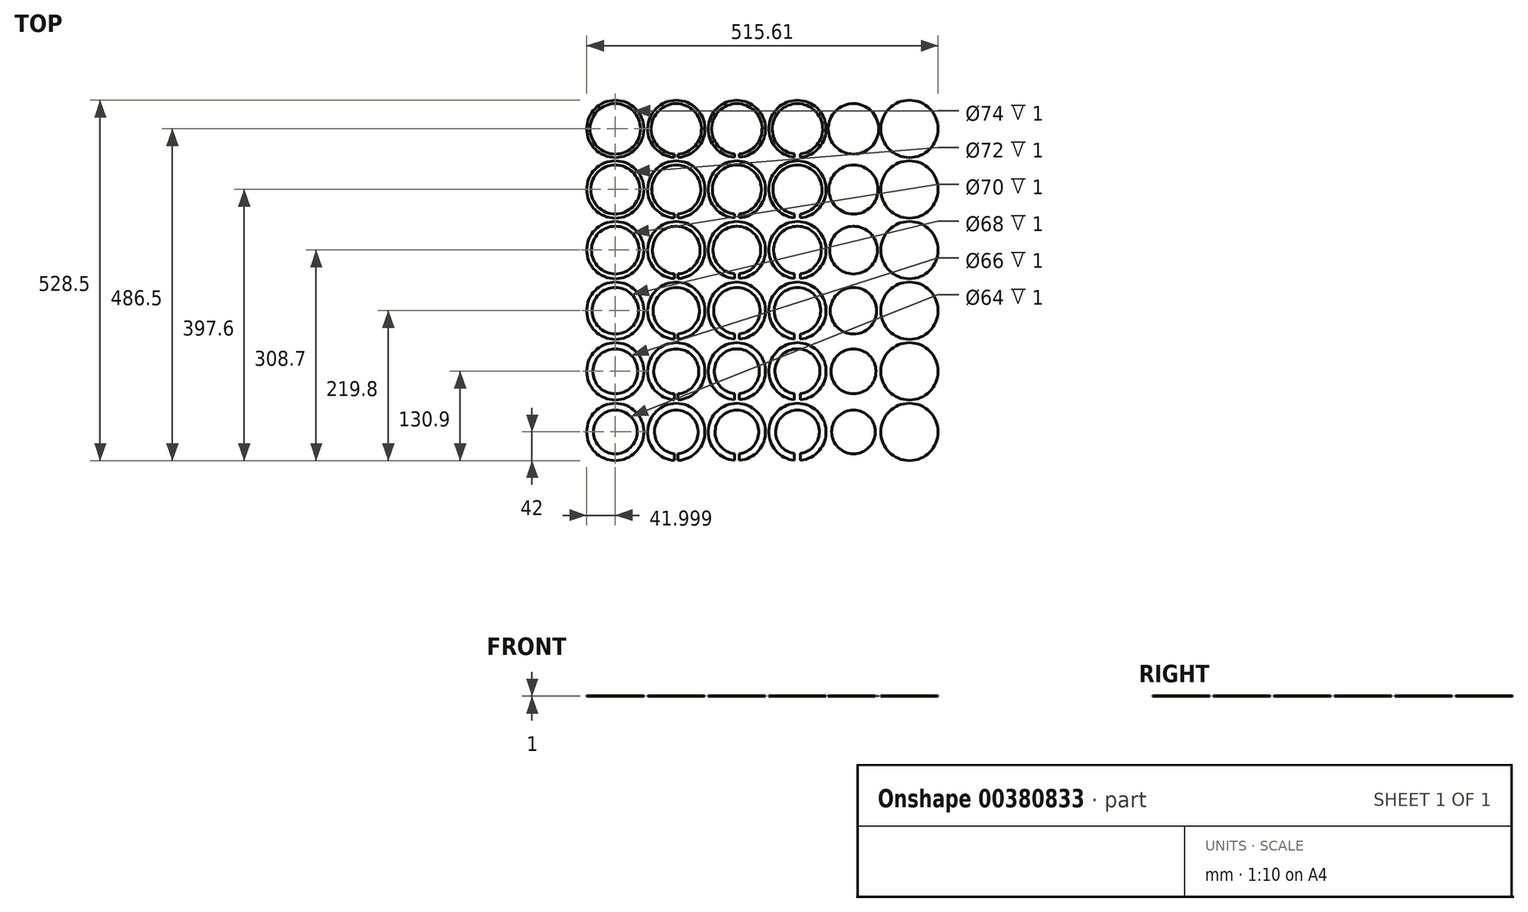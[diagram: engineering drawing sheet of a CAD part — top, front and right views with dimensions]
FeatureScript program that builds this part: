
annotation { "Feature Type Name" : "Feature", "Feature Type Description" : "" }
export const myFeature = defineFeature(function(context is Context, id is Id, definition is map)
    precondition{}
    {
        {
            var Q0;
            Q0=qCreatedBy(makeId("Top.planeOp"),FACE);
            var sketch = newSketch(context, id + "F0", { "sketchPlane" : qUnion([Q0])});
            skArc(sketch, "E0", {"start": v(2.5, -41.93) * mm, "mid": v(0, 42) * mm, "end": v(-2.5, -41.93) * mm});
            skArc(sketch, "E1", {"start": v(2.5, -36.92) * mm, "mid": v(0, 37) * mm, "end": v(-2.5, -36.92) * mm});
            skArc(sketch, "E2", {"start": v(92.4, -41.85) * mm, "mid": v(88.9, 42) * mm, "end": v(85.4, -41.85) * mm});
            skArc(sketch, "E3", {"start": v(92.4, -36.83) * mm, "mid": v(88.9, 37) * mm, "end": v(85.4, -36.83) * mm});
            skArc(sketch, "E4", {"start": v(182.3, -41.76) * mm, "mid": v(177.8, 42) * mm, "end": v(173.3, -41.76) * mm});
            skArc(sketch, "E5", {"start": v(182.3, -36.73) * mm, "mid": v(177.8, 37) * mm, "end": v(173.3, -36.73) * mm});
            skLineSegment(sketch, "E6", {"start": v(0, 0) * mm, "end": v(88.9, 0) * mm, "construction": true});
            skLineSegment(sketch, "E7", {"start": v(88.9, 0) * mm, "end": v(177.8, 0) * mm, "construction": true});
            skLineSegment(sketch, "E8", {"start": v(0, 0) * mm, "end": v(0, -42) * mm, "construction": true});
            skLineSegment(sketch, "E9", {"start": v(-2.5, -36.92) * mm, "end": v(-2.5, -41.93) * mm});
            skLineSegment(sketch, "E10", {"start": v(2.5, -36.92) * mm, "end": v(2.5, -41.93) * mm});
            skLineSegment(sketch, "E11", {"start": v(88.9, 0) * mm, "end": v(88.9, -42) * mm, "construction": true});
            skLineSegment(sketch, "E12", {"start": v(177.8, 0) * mm, "end": v(177.8, -42) * mm, "construction": true});
            skLineSegment(sketch, "E13", {"start": v(85.4, -36.83) * mm, "end": v(85.4, -41.85) * mm});
            skLineSegment(sketch, "E14", {"start": v(92.4, -36.83) * mm, "end": v(92.4, -41.85) * mm});
            skLineSegment(sketch, "E15", {"start": v(173.3, -36.73) * mm, "end": v(173.3, -41.76) * mm});
            skLineSegment(sketch, "E16", {"start": v(182.3, -36.73) * mm, "end": v(182.3, -41.76) * mm});
            skLineSegment(sketch, "E17.0.1.0", {"start": v(0, -88.9) * mm, "end": v(88.9, -88.9) * mm, "construction": true});
            skLineSegment(sketch, "E17.0.1.1", {"start": v(0, -88.9) * mm, "end": v(0, -130.9) * mm, "construction": true});
            skLineSegment(sketch, "E17.0.1.2", {"start": v(88.9, -88.9) * mm, "end": v(88.9, -130.9) * mm, "construction": true});
            skLineSegment(sketch, "E17.0.1.3", {"start": v(88.9, -88.9) * mm, "end": v(177.8, -88.9) * mm, "construction": true});
            skCircle(sketch, "E17.0.1.4", {"center": v(88.9, -88.9) * mm, "radius": 37 * mm, "construction": true});
            skLineSegment(sketch, "E17.0.1.5", {"start": v(177.8, -88.9) * mm, "end": v(177.8, -130.9) * mm, "construction": true});
            skArc(sketch, "E17.0.1.6", {"start": v(92.4, -130.75) * mm, "mid": v(88.9, -46.9) * mm, "end": v(85.4, -130.75) * mm});
            skCircle(sketch, "E17.0.1.7", {"center": v(177.8, -88.9) * mm, "radius": 37 * mm, "construction": true});
            skArc(sketch, "E17.0.1.8", {"start": v(182.3, -130.66) * mm, "mid": v(177.8, -46.9) * mm, "end": v(173.3, -130.66) * mm});
            skCircle(sketch, "E17.0.1.9", {"center": v(0, -88.9) * mm, "radius": 37 * mm, "construction": true});
            skArc(sketch, "E17.0.1.10", {"start": v(2.5, -130.83) * mm, "mid": v(0, -46.9) * mm, "end": v(-2.5, -130.83) * mm});
            skLineSegment(sketch, "E17.0.1.11", {"start": v(92.4, -124.73) * mm, "end": v(92.4, -130.75) * mm});
            skLineSegment(sketch, "E17.0.1.12", {"start": v(85.4, -124.73) * mm, "end": v(85.4, -130.75) * mm});
            skLineSegment(sketch, "E17.0.1.13", {"start": v(2.5, -124.81) * mm, "end": v(2.5, -130.83) * mm});
            skLineSegment(sketch, "E17.0.1.14", {"start": v(173.3, -124.62) * mm, "end": v(173.3, -130.66) * mm});
            skLineSegment(sketch, "E17.0.1.15", {"start": v(182.3, -124.62) * mm, "end": v(182.3, -130.66) * mm});
            skLineSegment(sketch, "E17.0.1.16", {"start": v(-2.5, -125.82) * mm, "end": v(-2.5, -130.83) * mm});
            skLineSegment(sketch, "E17.0.2.0", {"start": v(0, -177.8) * mm, "end": v(88.9, -177.8) * mm, "construction": true});
            skLineSegment(sketch, "E17.0.2.1", {"start": v(0, -177.8) * mm, "end": v(0, -219.8) * mm, "construction": true});
            skLineSegment(sketch, "E17.0.2.2", {"start": v(88.9, -177.8) * mm, "end": v(88.9, -219.8) * mm, "construction": true});
            skLineSegment(sketch, "E17.0.2.3", {"start": v(88.9, -177.8) * mm, "end": v(177.8, -177.8) * mm, "construction": true});
            skCircle(sketch, "E17.0.2.4", {"center": v(88.9, -177.8) * mm, "radius": 37 * mm, "construction": true});
            skLineSegment(sketch, "E17.0.2.5", {"start": v(177.8, -177.8) * mm, "end": v(177.8, -219.8) * mm, "construction": true});
            skArc(sketch, "E17.0.2.6", {"start": v(92.4, -219.65) * mm, "mid": v(88.9, -135.8) * mm, "end": v(85.4, -219.65) * mm});
            skCircle(sketch, "E17.0.2.7", {"center": v(177.8, -177.8) * mm, "radius": 37 * mm, "construction": true});
            skArc(sketch, "E17.0.2.8", {"start": v(182.3, -219.56) * mm, "mid": v(177.8, -135.8) * mm, "end": v(173.3, -219.56) * mm});
            skCircle(sketch, "E17.0.2.9", {"center": v(0, -177.8) * mm, "radius": 37 * mm, "construction": true});
            skArc(sketch, "E17.0.2.10", {"start": v(2.5, -219.73) * mm, "mid": v(0, -135.8) * mm, "end": v(-2.5, -219.73) * mm});
            skLineSegment(sketch, "E17.0.2.11", {"start": v(92.4, -212.62) * mm, "end": v(92.4, -219.65) * mm});
            skLineSegment(sketch, "E17.0.2.12", {"start": v(85.4, -212.62) * mm, "end": v(85.4, -219.65) * mm});
            skLineSegment(sketch, "E17.0.2.13", {"start": v(2.5, -212.71) * mm, "end": v(2.5, -219.73) * mm});
            skLineSegment(sketch, "E17.0.2.14", {"start": v(173.3, -212.5) * mm, "end": v(173.3, -219.56) * mm});
            skLineSegment(sketch, "E17.0.2.15", {"start": v(182.3, -212.5) * mm, "end": v(182.3, -219.56) * mm});
            skLineSegment(sketch, "E17.0.2.16", {"start": v(-2.5, -212.71) * mm, "end": v(-2.5, -219.73) * mm});
            skLineSegment(sketch, "E17.0.3.0", {"start": v(0, -266.7) * mm, "end": v(88.9, -266.7) * mm, "construction": true});
            skLineSegment(sketch, "E17.0.3.1", {"start": v(0, -266.7) * mm, "end": v(0, -308.7) * mm, "construction": true});
            skLineSegment(sketch, "E17.0.3.2", {"start": v(88.9, -266.7) * mm, "end": v(88.9, -308.7) * mm, "construction": true});
            skLineSegment(sketch, "E17.0.3.3", {"start": v(88.9, -266.7) * mm, "end": v(177.8, -266.7) * mm, "construction": true});
            skCircle(sketch, "E17.0.3.4", {"center": v(88.9, -266.7) * mm, "radius": 37 * mm, "construction": true});
            skLineSegment(sketch, "E17.0.3.5", {"start": v(177.8, -266.7) * mm, "end": v(177.8, -308.7) * mm, "construction": true});
            skArc(sketch, "E17.0.3.6", {"start": v(92.4, -308.55) * mm, "mid": v(88.9, -224.7) * mm, "end": v(85.4, -308.55) * mm});
            skCircle(sketch, "E17.0.3.7", {"center": v(177.8, -266.7) * mm, "radius": 37 * mm, "construction": true});
            skArc(sketch, "E17.0.3.8", {"start": v(182.3, -308.46) * mm, "mid": v(177.8, -224.7) * mm, "end": v(173.3, -308.46) * mm});
            skCircle(sketch, "E17.0.3.9", {"center": v(0, -266.7) * mm, "radius": 37 * mm, "construction": true});
            skArc(sketch, "E17.0.3.10", {"start": v(2.5, -308.63) * mm, "mid": v(0, -224.7) * mm, "end": v(-2.5, -308.63) * mm});
            skLineSegment(sketch, "E17.0.3.11", {"start": v(92.4, -300.52) * mm, "end": v(92.4, -308.55) * mm});
            skLineSegment(sketch, "E17.0.3.12", {"start": v(85.4, -300.52) * mm, "end": v(85.4, -308.55) * mm});
            skLineSegment(sketch, "E17.0.3.13", {"start": v(2.5, -300.6) * mm, "end": v(2.5, -308.63) * mm});
            skLineSegment(sketch, "E17.0.3.14", {"start": v(173.3, -300.4) * mm, "end": v(173.3, -308.46) * mm});
            skLineSegment(sketch, "E17.0.3.15", {"start": v(182.3, -300.4) * mm, "end": v(182.3, -308.46) * mm});
            skLineSegment(sketch, "E17.0.3.16", {"start": v(-2.5, -300.6) * mm, "end": v(-2.5, -308.63) * mm});
            skLineSegment(sketch, "E17.0.4.0", {"start": v(0, -355.6) * mm, "end": v(88.9, -355.6) * mm, "construction": true});
            skLineSegment(sketch, "E17.0.4.1", {"start": v(0, -355.6) * mm, "end": v(0, -397.6) * mm, "construction": true});
            skLineSegment(sketch, "E17.0.4.2", {"start": v(88.9, -355.6) * mm, "end": v(88.9, -397.6) * mm, "construction": true});
            skLineSegment(sketch, "E17.0.4.3", {"start": v(88.9, -355.6) * mm, "end": v(177.8, -355.6) * mm, "construction": true});
            skCircle(sketch, "E17.0.4.4", {"center": v(88.9, -355.6) * mm, "radius": 37 * mm, "construction": true});
            skLineSegment(sketch, "E17.0.4.5", {"start": v(177.8, -355.6) * mm, "end": v(177.8, -397.6) * mm, "construction": true});
            skArc(sketch, "E17.0.4.6", {"start": v(92.4, -397.45) * mm, "mid": v(88.9, -313.6) * mm, "end": v(85.4, -397.45) * mm});
            skCircle(sketch, "E17.0.4.7", {"center": v(177.8, -355.6) * mm, "radius": 37 * mm, "construction": true});
            skArc(sketch, "E17.0.4.8", {"start": v(182.3, -397.36) * mm, "mid": v(177.8, -313.6) * mm, "end": v(173.3, -397.36) * mm});
            skCircle(sketch, "E17.0.4.9", {"center": v(0, -355.6) * mm, "radius": 37 * mm, "construction": true});
            skArc(sketch, "E17.0.4.10", {"start": v(2.5, -397.53) * mm, "mid": v(0, -313.6) * mm, "end": v(-2.5, -397.53) * mm});
            skLineSegment(sketch, "E17.0.4.11", {"start": v(92.4, -388.41) * mm, "end": v(92.4, -397.45) * mm});
            skLineSegment(sketch, "E17.0.4.12", {"start": v(85.4, -388.41) * mm, "end": v(85.4, -397.45) * mm});
            skLineSegment(sketch, "E17.0.4.13", {"start": v(2.5, -388.5) * mm, "end": v(2.5, -397.53) * mm});
            skLineSegment(sketch, "E17.0.4.14", {"start": v(173.3, -388.3) * mm, "end": v(173.3, -397.36) * mm});
            skLineSegment(sketch, "E17.0.4.15", {"start": v(182.3, -388.3) * mm, "end": v(182.3, -397.36) * mm});
            skLineSegment(sketch, "E17.0.4.16", {"start": v(-2.5, -388.5) * mm, "end": v(-2.5, -397.53) * mm});
            skLineSegment(sketch, "E17.0.5.0", {"start": v(0, -444.5) * mm, "end": v(88.9, -444.5) * mm, "construction": true});
            skLineSegment(sketch, "E17.0.5.1", {"start": v(0, -444.5) * mm, "end": v(0, -486.5) * mm, "construction": true});
            skLineSegment(sketch, "E17.0.5.2", {"start": v(88.9, -444.5) * mm, "end": v(88.9, -486.5) * mm, "construction": true});
            skLineSegment(sketch, "E17.0.5.3", {"start": v(88.9, -444.5) * mm, "end": v(177.8, -444.5) * mm, "construction": true});
            skCircle(sketch, "E17.0.5.4", {"center": v(88.9, -444.5) * mm, "radius": 37 * mm, "construction": true});
            skLineSegment(sketch, "E17.0.5.5", {"start": v(177.8, -444.5) * mm, "end": v(177.8, -486.5) * mm, "construction": true});
            skArc(sketch, "E17.0.5.6", {"start": v(92.4, -486.35) * mm, "mid": v(88.9, -402.5) * mm, "end": v(85.4, -486.35) * mm});
            skCircle(sketch, "E17.0.5.7", {"center": v(177.8, -444.5) * mm, "radius": 37 * mm, "construction": true});
            skArc(sketch, "E17.0.5.8", {"start": v(182.3, -486.26) * mm, "mid": v(177.8, -402.5) * mm, "end": v(173.3, -486.26) * mm});
            skCircle(sketch, "E17.0.5.9", {"center": v(0, -444.5) * mm, "radius": 37 * mm, "construction": true});
            skArc(sketch, "E17.0.5.10", {"start": v(2.5, -486.43) * mm, "mid": v(0, -402.5) * mm, "end": v(-2.5, -486.43) * mm});
            skLineSegment(sketch, "E17.0.5.11", {"start": v(92.4, -476.3) * mm, "end": v(92.4, -486.35) * mm});
            skLineSegment(sketch, "E17.0.5.12", {"start": v(85.4, -476.3) * mm, "end": v(85.4, -486.35) * mm});
            skLineSegment(sketch, "E17.0.5.13", {"start": v(2.5, -476.4) * mm, "end": v(2.5, -486.43) * mm});
            skLineSegment(sketch, "E17.0.5.14", {"start": v(173.3, -476.18) * mm, "end": v(173.3, -486.26) * mm});
            skLineSegment(sketch, "E17.0.5.15", {"start": v(182.3, -476.18) * mm, "end": v(182.3, -486.26) * mm});
            skLineSegment(sketch, "E17.0.5.16", {"start": v(-2.5, -476.4) * mm, "end": v(-2.5, -486.43) * mm});
            skLineSegment(sketch, "E17.direction1", {"start": v(2.5, -41.93) * mm, "end": v(22.9, -41.93) * mm, "construction": true});
            skLineSegment(sketch, "E17.direction2", {"start": v(-2.5, -41.93) * mm, "end": v(-2.5, -130.83) * mm, "construction": true});
            skArc(sketch, "E18", {"start": v(2.5, -124.81) * mm, "mid": v(0, -52.9) * mm, "end": v(-2.5, -124.81) * mm});
            skArc(sketch, "E19", {"start": v(92.4, -124.73) * mm, "mid": v(88.9, -52.9) * mm, "end": v(85.4, -124.73) * mm});
            skArc(sketch, "E20", {"start": v(182.3, -124.62) * mm, "mid": v(177.8, -52.9) * mm, "end": v(173.3, -124.62) * mm});
            skArc(sketch, "E21", {"start": v(182.3, -212.5) * mm, "mid": v(177.8, -142.8) * mm, "end": v(173.3, -212.5) * mm});
            skArc(sketch, "E22", {"start": v(92.4, -212.62) * mm, "mid": v(88.9, -142.8) * mm, "end": v(85.4, -212.62) * mm});
            skArc(sketch, "E23", {"start": v(2.5, -212.71) * mm, "mid": v(0, -142.8) * mm, "end": v(-2.5, -212.71) * mm});
            skArc(sketch, "E24", {"start": v(2.5, -300.6) * mm, "mid": v(0, -232.7) * mm, "end": v(-2.5, -300.6) * mm});
            skArc(sketch, "E25", {"start": v(92.4, -300.52) * mm, "mid": v(88.9, -232.7) * mm, "end": v(85.4, -300.52) * mm});
            skArc(sketch, "E26", {"start": v(182.3, -300.4) * mm, "mid": v(177.8, -232.7) * mm, "end": v(173.3, -300.4) * mm});
            skArc(sketch, "E27", {"start": v(182.3, -388.3) * mm, "mid": v(177.8, -322.6) * mm, "end": v(173.3, -388.3) * mm});
            skArc(sketch, "E28", {"start": v(92.4, -388.41) * mm, "mid": v(88.9, -322.6) * mm, "end": v(85.4, -388.41) * mm});
            skArc(sketch, "E29", {"start": v(2.5, -388.5) * mm, "mid": v(0, -322.6) * mm, "end": v(-2.5, -388.5) * mm});
            skArc(sketch, "E30", {"start": v(2.5, -476.4) * mm, "mid": v(0, -412.5) * mm, "end": v(-2.5, -476.4) * mm});
            skArc(sketch, "E31", {"start": v(92.4, -476.3) * mm, "mid": v(88.9, -412.5) * mm, "end": v(85.4, -476.3) * mm});
            skArc(sketch, "E32", {"start": v(182.3, -476.18) * mm, "mid": v(177.8, -412.5) * mm, "end": v(173.3, -476.18) * mm});
            skPoint(sketch, "E33.orphan", {"position": v(2.5, -125.82) * mm});
            skLineSegment(sketch, "E34", {"start": v(-2.5, -125.82) * mm, "end": v(-2.5, -124.81) * mm});
            skPoint(sketch, "E35.orphan", {"position": v(85.4, -125.73) * mm});
            skPoint(sketch, "E36.orphan", {"position": v(92.4, -125.73) * mm});
            skPoint(sketch, "E37.orphan", {"position": v(173.3, -125.63) * mm});
            skPoint(sketch, "E38.orphan", {"position": v(182.3, -125.63) * mm});
            skPoint(sketch, "E39.orphan", {"position": v(-2.5, -214.72) * mm});
            skPoint(sketch, "E40.orphan", {"position": v(2.5, -214.72) * mm});
            skPoint(sketch, "E41.orphan", {"position": v(85.4, -214.63) * mm});
            skPoint(sketch, "E42.orphan", {"position": v(92.4, -214.63) * mm});
            skPoint(sketch, "E43.orphan", {"position": v(173.3, -214.53) * mm});
            skPoint(sketch, "E44.orphan", {"position": v(182.3, -214.53) * mm});
            skPoint(sketch, "E45.orphan", {"position": v(182.3, -303.43) * mm});
            skPoint(sketch, "E46.orphan", {"position": v(173.3, -303.43) * mm});
            skPoint(sketch, "E47.orphan", {"position": v(92.4, -303.53) * mm});
            skPoint(sketch, "E48.orphan", {"position": v(85.4, -303.53) * mm});
            skPoint(sketch, "E49.orphan", {"position": v(-2.5, -303.62) * mm});
            skPoint(sketch, "E50.orphan", {"position": v(2.5, -303.62) * mm});
            skPoint(sketch, "E51.orphan", {"position": v(-2.5, -392.52) * mm});
            skPoint(sketch, "E52.orphan", {"position": v(2.5, -392.52) * mm});
            skPoint(sketch, "E53.orphan", {"position": v(85.4, -392.43) * mm});
            skPoint(sketch, "E54.orphan", {"position": v(92.4, -392.43) * mm});
            skPoint(sketch, "E55.orphan", {"position": v(182.3, -392.33) * mm});
            skPoint(sketch, "E56.orphan", {"position": v(173.3, -392.33) * mm});
            skPoint(sketch, "E57.orphan", {"position": v(-2.5, -481.42) * mm});
            skPoint(sketch, "E58.orphan", {"position": v(2.5, -481.42) * mm});
            skPoint(sketch, "E59.orphan", {"position": v(85.4, -481.33) * mm});
            skPoint(sketch, "E60.orphan", {"position": v(92.4, -481.33) * mm});
            skPoint(sketch, "E61.orphan", {"position": v(173.3, -481.23) * mm});
            skPoint(sketch, "E62.orphan", {"position": v(182.3, -481.23) * mm});
            skSolve(sketch);
        }
        {
            var Q0;
            Q0 = qSketchRegion(id + "F0", true);
            extrude(context, id + "F1", {"entities" : qUnion([Q0]), "depth" : 1 * mm});
        }
        {
            var Q0;
            Q0=qCreatedBy(makeId("Top.planeOp"),FACE);
            var sketch = newSketch(context, id + "F2", { "sketchPlane" : qUnion([Q0])});
            skCircle(sketch, "E63", {"center": v(259.98, 0) * mm, "radius": 37 * mm});
            skCircle(sketch, "E64", {"center": v(342.15, 0) * mm, "radius": 42 * mm});
            skCircle(sketch, "E65.0.1.0", {"center": v(342.15, -88.9) * mm, "radius": 42 * mm});
            skCircle(sketch, "E65.0.2.0", {"center": v(342.15, -177.8) * mm, "radius": 42 * mm});
            skCircle(sketch, "E65.0.3.0", {"center": v(342.15, -266.7) * mm, "radius": 42 * mm});
            skCircle(sketch, "E65.0.4.0", {"center": v(342.15, -355.6) * mm, "radius": 42 * mm});
            skCircle(sketch, "E65.0.5.0", {"center": v(342.15, -444.5) * mm, "radius": 42 * mm});
            skLineSegment(sketch, "E65.direction1", {"start": v(342.15, 0) * mm, "end": v(367.55, 0) * mm, "construction": true});
            skLineSegment(sketch, "E65.direction2", {"start": v(342.15, 0) * mm, "end": v(342.15, -88.9) * mm, "construction": true});
            skCircle(sketch, "E66", {"center": v(259.98, -88.9) * mm, "radius": 36 * mm});
            skCircle(sketch, "E67", {"center": v(259.98, -177.8) * mm, "radius": 35 * mm});
            skCircle(sketch, "E68", {"center": v(259.98, -266.7) * mm, "radius": 34 * mm});
            skCircle(sketch, "E69", {"center": v(259.98, -355.6) * mm, "radius": 33 * mm});
            skCircle(sketch, "E70", {"center": v(259.98, -444.5) * mm, "radius": 32 * mm});
            skSolve(sketch);
        }
        {
            var Q0;
            Q0 = qSketchRegion(id + "F2", true);
            extrude(context, id + "F3", {"entities" : qUnion([Q0]), "depth" : 1 * mm});
        }
        {
            var Q0;
            Q0=qCreatedBy(makeId("Top.planeOp"),FACE);
            var sketch = newSketch(context, id + "F4", { "sketchPlane" : qUnion([Q0])});
            skCircle(sketch, "E71", {"center": v(-89.46, 0) * mm, "radius": 42 * mm});
            skCircle(sketch, "E72", {"center": v(-89.46, 0) * mm, "radius": 37 * mm});
            skCircle(sketch, "E73.0.1.0", {"center": v(-89.46, -88.9) * mm, "radius": 42 * mm});
            skCircle(sketch, "E73.0.2.0", {"center": v(-89.46, -177.8) * mm, "radius": 42 * mm});
            skCircle(sketch, "E73.0.3.0", {"center": v(-89.46, -266.7) * mm, "radius": 42 * mm});
            skCircle(sketch, "E73.0.4.0", {"center": v(-89.46, -355.6) * mm, "radius": 42 * mm});
            skCircle(sketch, "E73.0.5.0", {"center": v(-89.46, -444.5) * mm, "radius": 42 * mm});
            skLineSegment(sketch, "E73.direction1", {"start": v(-89.46, 0) * mm, "end": v(-64.06, 0) * mm, "construction": true});
            skLineSegment(sketch, "E73.direction2", {"start": v(-89.46, 0) * mm, "end": v(-89.46, -88.9) * mm, "construction": true});
            skCircle(sketch, "E74", {"center": v(-89.46, -88.9) * mm, "radius": 36 * mm});
            skCircle(sketch, "E75", {"center": v(-89.46, -177.8) * mm, "radius": 35 * mm});
            skCircle(sketch, "E76", {"center": v(-89.46, -266.7) * mm, "radius": 34 * mm});
            skCircle(sketch, "E77", {"center": v(-89.46, -355.6) * mm, "radius": 33 * mm});
            skCircle(sketch, "E78", {"center": v(-89.46, -444.5) * mm, "radius": 32 * mm});
            skSolve(sketch);
        }
        {
            var Q0;
            Q0 = qSketchRegion(id + "F4", true);
            extrude(context, id + "F5", {"entities" : qUnion([Q0]), "depth" : 1 * mm});
        }
    });
